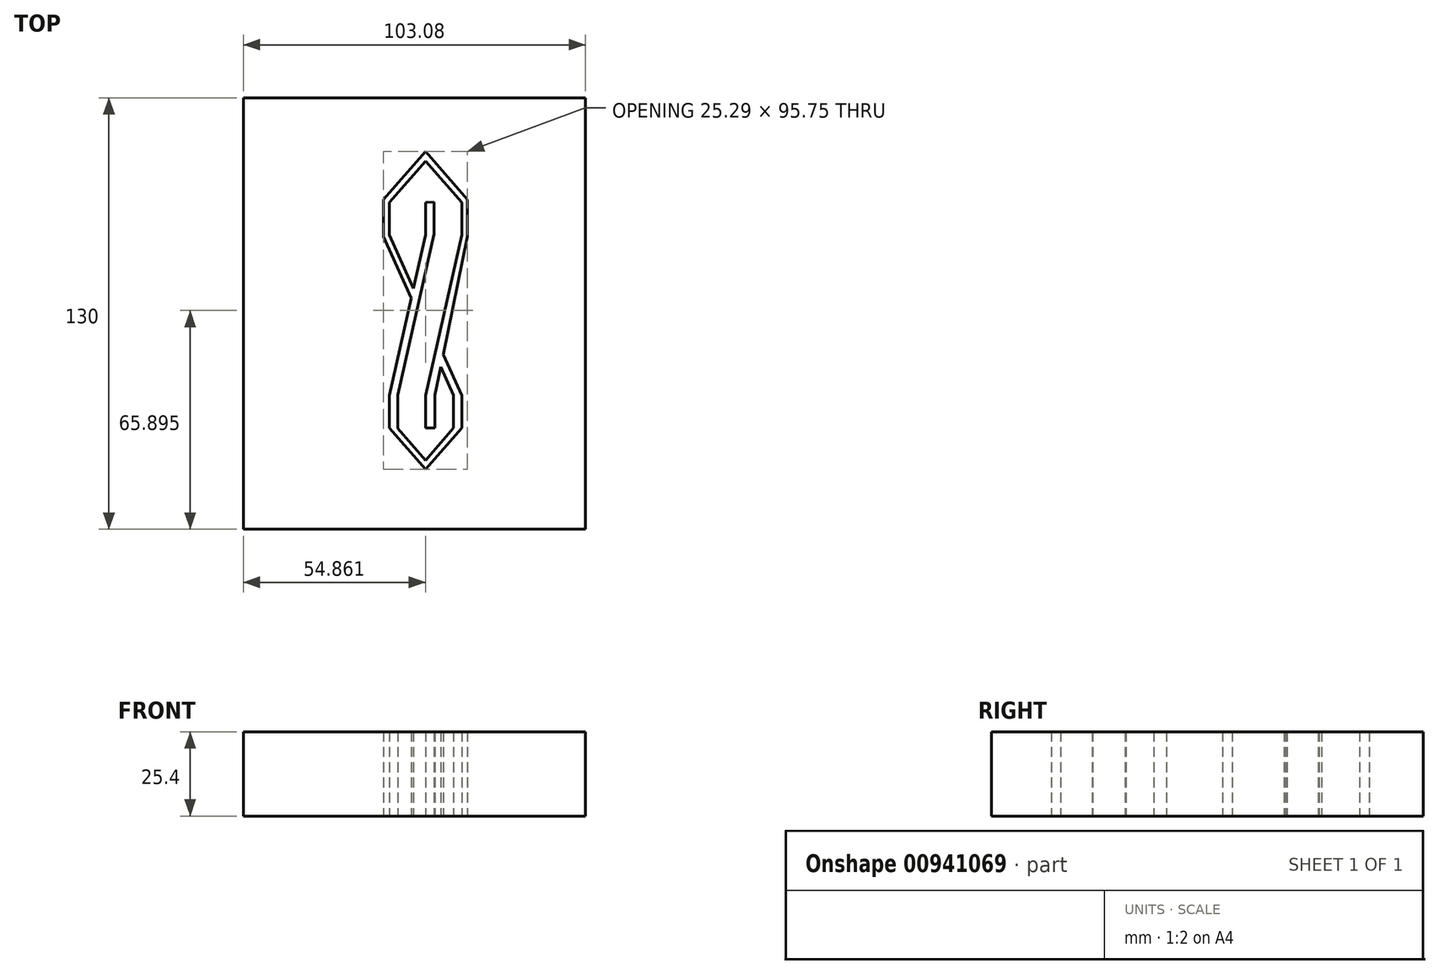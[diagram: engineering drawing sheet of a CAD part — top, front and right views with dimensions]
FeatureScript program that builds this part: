
annotation { "Feature Type Name" : "Feature", "Feature Type Description" : "" }
export const myFeature = defineFeature(function(context is Context, id is Id, definition is map)
    precondition{}
    {
        {
            var Q0;
            Q0=qCreatedBy(makeId("Top.planeOp"),FACE);
            var sketch = newSketch(context, id + "F0", { "sketchPlane" : qUnion([Q0])});
            skLineSegment(sketch, "E0", {"start": v(-10.92, 33.97) * mm, "end": v(-10.92, 24.21) * mm});
            skLineSegment(sketch, "E1", {"start": v(0, 33.97) * mm, "end": v(0, 24.21) * mm});
            skLineSegment(sketch, "E2.MirrorCS", {"start": v(10.92, 33.97) * mm, "end": v(10.92, 24.21) * mm});
            skLineSegment(sketch, "E3.MirrorCS", {"start": v(-10.92, -33.97) * mm, "end": v(-10.92, -24.21) * mm});
            skLineSegment(sketch, "E4.MirrorCS", {"start": v(0, -33.97) * mm, "end": v(0, -24.21) * mm});
            skLineSegment(sketch, "E5.MirrorCS", {"start": v(10.92, -33.97) * mm, "end": v(10.92, -24.21) * mm});
            skLineSegment(sketch, "E6", {"start": v(-10.92, 33.97) * mm, "end": v(0, 46.4) * mm});
            skLineSegment(sketch, "E7", {"start": v(0, 46.4) * mm, "end": v(10.92, 33.97) * mm});
            skLineSegment(sketch, "E8", {"start": v(10.92, 24.21) * mm, "end": v(0, -24.21) * mm});
            skLineSegment(sketch, "E9", {"start": v(0, 24.21) * mm, "end": v(-10.92, -24.21) * mm});
            skLineSegment(sketch, "E10", {"start": v(-10.92, 24.21) * mm, "end": v(-3.64, 8.07) * mm});
            skLineSegment(sketch, "E11.MirrorCS", {"start": v(-10.92, -33.97) * mm, "end": v(0, -46.4) * mm});
            skLineSegment(sketch, "E12.MirrorCS", {"start": v(0, -46.4) * mm, "end": v(10.92, -33.97) * mm});
            skLineSegment(sketch, "E13", {"start": v(-8.41, -34.1) * mm, "end": v(-8.41, -24) * mm});
            skLineSegment(sketch, "E14", {"start": v(-8.41, -34.1) * mm, "end": v(0, -43.7) * mm});
            skLineSegment(sketch, "E15", {"start": v(0, -43.7) * mm, "end": v(8.38, -33.97) * mm});
            skLineSegment(sketch, "E16", {"start": v(8.38, -33.97) * mm, "end": v(8.38, -24) * mm});
            skLineSegment(sketch, "E17", {"start": v(8.38, -24) * mm, "end": v(4.56, -15.54) * mm});
            skLineSegment(sketch, "E18", {"start": v(-4.3, 5.14) * mm, "end": v(-12.66, 23.7) * mm});
            skLineSegment(sketch, "E19", {"start": v(-12.66, 23.7) * mm, "end": v(-12.66, 34.95) * mm});
            skLineSegment(sketch, "E20", {"start": v(-12.66, 34.95) * mm, "end": v(0, 49.34) * mm});
            skLineSegment(sketch, "E21", {"start": v(0, 49.34) * mm, "end": v(12.63, 34.95) * mm});
            skLineSegment(sketch, "E22", {"start": v(12.63, 34.95) * mm, "end": v(12.63, 23.7) * mm});
            skLineSegment(sketch, "E23", {"start": v(12.63, 23.7) * mm, "end": v(2.82, -24) * mm});
            skLineSegment(sketch, "E24", {"start": v(2.82, -24) * mm, "end": v(2.82, -33.97) * mm});
            skLineSegment(sketch, "E25", {"start": v(2.82, -33.97) * mm, "end": v(0, -33.97) * mm});
            skLineSegment(sketch, "E26", {"start": v(2.52, 24.48) * mm, "end": v(2.52, 34.15) * mm});
            skLineSegment(sketch, "E27", {"start": v(0, 33.97) * mm, "end": v(2.52, 34.15) * mm});
            skLineSegment(sketch, "E28", {"start": v(2.52, 24.48) * mm, "end": v(-8.41, -24) * mm});
            skLineSegment(sketch, "E29", {"start": v(5.33, -11.82) * mm, "end": v(10.92, -24.21) * mm});
            skSolve(sketch);
        }
        {
            var Q0;
            Q0=qCreatedBy(makeId("Top.planeOp"),FACE);
            var sketch = newSketch(context, id + "F1", { "sketchPlane" : qUnion([Q0])});
            skLineSegment(sketch, "E30.bottom", {"start": v(-54.88, -64.43) * mm, "end": v(48.2, -64.43) * mm});
            skLineSegment(sketch, "E30.top", {"start": v(-54.88, 65.57) * mm, "end": v(48.2, 65.57) * mm});
            skLineSegment(sketch, "E30.left", {"start": v(-54.88, -64.43) * mm, "end": v(-54.88, 65.57) * mm});
            skLineSegment(sketch, "E30.right", {"start": v(48.2, -64.43) * mm, "end": v(48.2, 65.57) * mm});
            skSolve(sketch);
        }
        {
            var Q0;
            Q0=makeQuery(id+"F1.imprint","IMPRINT",FACE,{"disambiguationData":[TD([[makeQuery(id+"F1.imprint","IMPRINT",EDGE,{"derivedFrom":sQuery(id+"F1.wireOp",EDGE,"E30.bottom")}),1.0]])]});
            extrude(context, id + "F2", {"entities" : qUnion([Q0]), "depth" : 25.4 * mm, "offsetDistance" : 25.4 * mm});
        }
        {
            var Q0;
            {var subQ5=sQuery(id+"F0.wireOp",EDGE,"E1");Q0=makeQuery(id+"F0.imprint","IMPRINT",FACE,{"disambiguationData":[TD([[makeQuery(id+"F0.imprint","IMPRINT",EDGE,{"derivedFrom":subQ5}),1.0]])]});}
            var Q1;
            Q1=makeQuery(id+"F0.imprint","IMPRINT",FACE,{"disambiguationData":[TD([[makeQuery(id+"F0.imprint","IMPRINT",EDGE,{"derivedFrom":sQuery(id+"F0.wireOp",EDGE,"E0")}),-1.0]])]});
            extrude(context, id + "F3", {"entities" : qUnion([Q0, Q1]), "operationType" : NewBodyOperationType.REMOVE, "depth" : 43.69 * mm, "offsetDistance" : 25.4 * mm});
        }
    });
